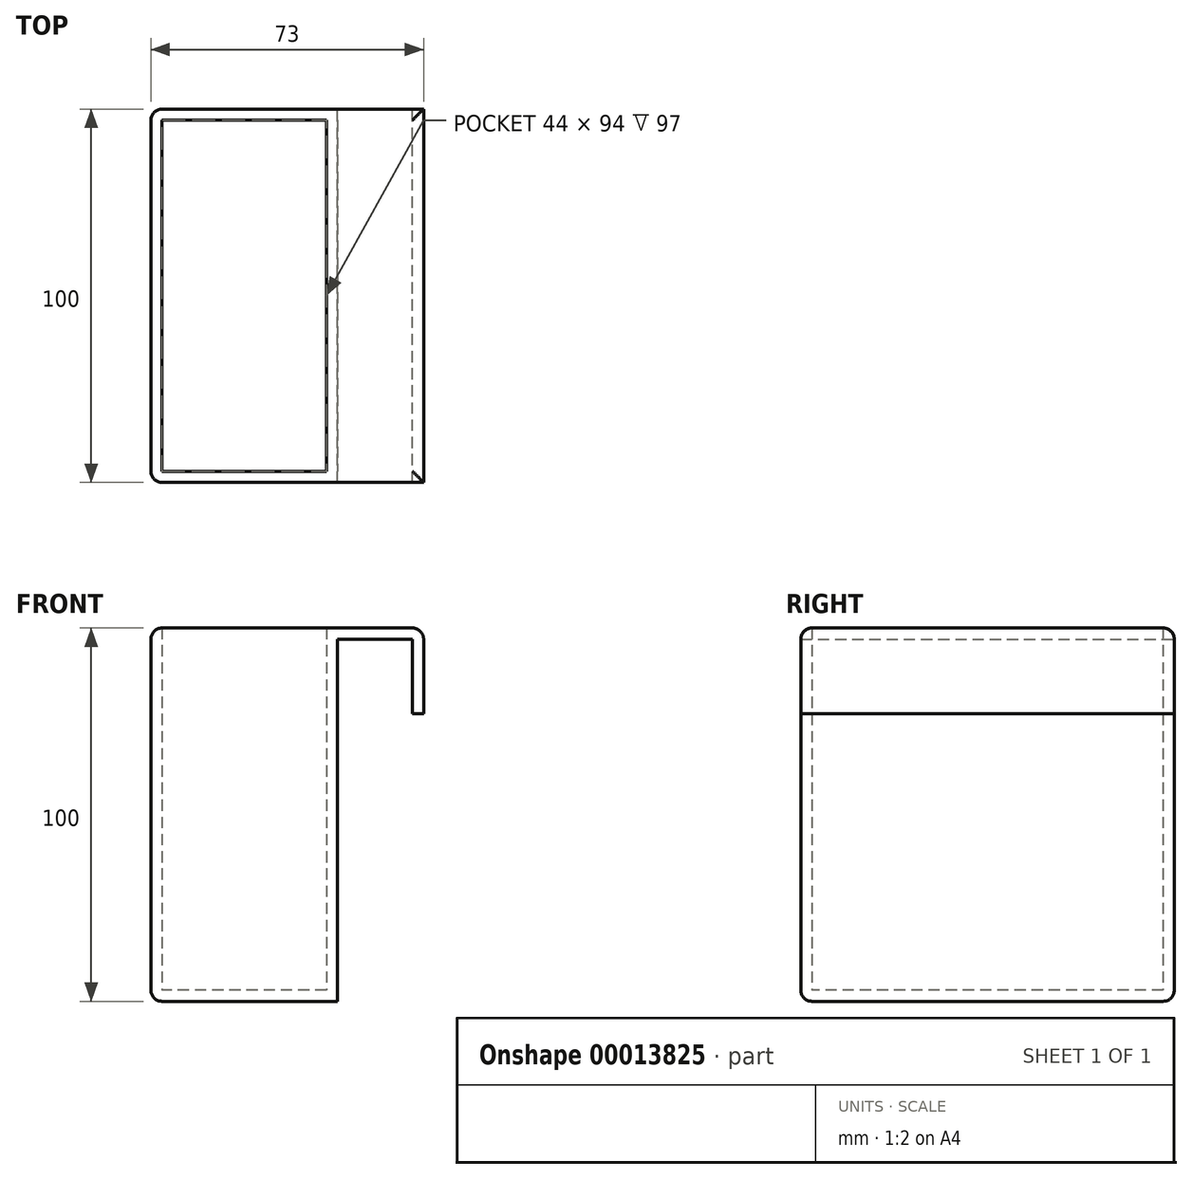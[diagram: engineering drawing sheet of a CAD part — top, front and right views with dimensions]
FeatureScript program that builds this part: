
annotation { "Feature Type Name" : "Feature", "Feature Type Description" : "" }
export const myFeature = defineFeature(function(context is Context, id is Id, definition is map)
    precondition{}
    {
        {
            var Q0;
            Q0=qCreatedBy(makeId("Top.planeOp"),FACE);
            var sketch = newSketch(context, id + "F0", { "sketchPlane" : qUnion([Q0])});
            skLineSegment(sketch, "E0.bottom", {"start": v(0, 0) * mm, "end": v(-50, 0) * mm});
            skLineSegment(sketch, "E0.top", {"start": v(0, -100) * mm, "end": v(-50, -100) * mm});
            skLineSegment(sketch, "E0.left", {"start": v(0, 0) * mm, "end": v(0, -100) * mm});
            skLineSegment(sketch, "E0.right", {"start": v(-50, 0) * mm, "end": v(-50, -100) * mm});
            skSolve(sketch);
        }
        {
            var Q0;
            Q0=makeQuery(id+"F0.imprint","IMPRINT",FACE,{"disambiguationData":[TD([[makeQuery(id+"F0.imprint","IMPRINT",EDGE,{"derivedFrom":sQuery(id+"F0.wireOp",EDGE,"E0.bottom")}),1.0]])]});
            extrude(context, id + "F1", {"entities" : qUnion([Q0]), "depth" : 100 * mm});
        }
        {
            var Q0;
            Q0=makeQuery(id+"F1.opExtrude","CAP_FACE",FACE,{"disambiguationData":[OSD([sQuery(id+"F0.wireOp",EDGE,"E0.bottom"),sQuery(id+"F0.wireOp",EDGE,"E0.top"),sQuery(id+"F0.wireOp",EDGE,"E0.left"),sQuery(id+"F0.wireOp",EDGE,"E0.right")])],"isStart":false});
            shell(context, id + "F2", {"entities" : qUnion([Q0]), "thickness" : 3 * mm});
        }
        {
            var Q0;
            Q0=makeQuery(id+"F1.opExtrude","SWEPT_FACE",FACE,{"disambiguationData":[OSD([sQuery(id+"F0.wireOp",EDGE,"E0.left")])]});
            var sketch = newSketch(context, id + "F3", { "sketchPlane" : qUnion([Q0])});
            skLineSegment(sketch, "E1.bottom", {"start": v(-100, 100) * mm, "end": v(0, 100) * mm});
            skLineSegment(sketch, "E1.top", {"start": v(-100, 97) * mm, "end": v(0, 97) * mm});
            skLineSegment(sketch, "E1.left", {"start": v(-100, 100) * mm, "end": v(-100, 97) * mm});
            skLineSegment(sketch, "E1.right", {"start": v(0, 100) * mm, "end": v(0, 97) * mm});
            skSolve(sketch);
        }
        {
            var Q0;
            Q0 = qSketchRegion(id + "F3", true);
            extrude(context, id + "F4", {"entities" : qUnion([Q0]), "operationType" : NewBodyOperationType.ADD, "depth" : 23 * mm});
        }
        {
            var Q0;
            Q0=makeQuery(id+"F4.opExtrude","SWEPT_FACE",FACE,{"disambiguationData":[OSD([sQuery(id+"F3.wireOp",EDGE,"E1.top")])]});
            var sketch = newSketch(context, id + "F5", { "sketchPlane" : qUnion([Q0])});
            skLineSegment(sketch, "E2.bottom", {"start": v(23, 100) * mm, "end": v(20, 100) * mm});
            skLineSegment(sketch, "E2.top", {"start": v(23, 0) * mm, "end": v(20, 0) * mm});
            skLineSegment(sketch, "E2.left", {"start": v(23, 100) * mm, "end": v(23, 0) * mm});
            skLineSegment(sketch, "E2.right", {"start": v(20, 100) * mm, "end": v(20, 0) * mm});
            skSolve(sketch);
        }
        {
            var Q0;
            Q0=makeQuery(id+"F5.imprint","IMPRINT",FACE,{"disambiguationData":[TD([[makeQuery(id+"F5.imprint","IMPRINT",EDGE,{"derivedFrom":sQuery(id+"F5.wireOp",EDGE,"E2.bottom")}),1.0]])]});
            extrude(context, id + "F6", {"entities" : qUnion([Q0]), "operationType" : NewBodyOperationType.ADD, "depth" : 20 * mm});
        }
        {
            var Q0;
            Q0=makeQuery(id+"F1.opExtrude","SWEPT_EDGE",EDGE,{"disambiguationData":[OSD([sQuery(id+"F0.wireOp",EDGE,"E0.top"),sQuery(id+"F0.wireOp",EDGE,"E0.right")])]});
            var Q1;
            Q1=makeQuery(id+"F1.opExtrude","SWEPT_EDGE",EDGE,{"disambiguationData":[OSD([sQuery(id+"F0.wireOp",EDGE,"E0.bottom"),sQuery(id+"F0.wireOp",EDGE,"E0.right")])]});
            var Q2;
            Q2=makeQuery(id+"F1.opExtrude","CAP_EDGE",EDGE,{"disambiguationData":[OSD([sQuery(id+"F0.wireOp",EDGE,"E0.right")])],"isStart":true});
            var Q3;
            Q3=makeQuery(id+"F1.opExtrude","CAP_EDGE",EDGE,{"disambiguationData":[OSD([sQuery(id+"F0.wireOp",EDGE,"E0.top")])],"isStart":true});
            var Q4;
            Q4=makeQuery(id+"F1.opExtrude","CAP_EDGE",EDGE,{"disambiguationData":[OSD([sQuery(id+"F0.wireOp",EDGE,"E0.bottom")])],"isStart":true});
            var Q5;
            Q5=makeQuery(id+"F1.opExtrude","CAP_EDGE",EDGE,{"disambiguationData":[OSD([sQuery(id+"F0.wireOp",EDGE,"E0.right")])],"isStart":false});
            var Q6;
            Q6=makeQuery(id+"F4.boolean.opBoolean","MERGE",EDGE,{"derivedFrom":[makeQuery(id+"F1.opExtrude","CAP_EDGE",EDGE,{"disambiguationData":[OSD([sQuery(id+"F0.wireOp",EDGE,"E0.bottom")])],"isStart":false}),makeQuery(id+"F4.opExtrude","SWEPT_EDGE",EDGE,{"disambiguationData":[OSD([sQuery(id+"F3.wireOp",EDGE,"E1.bottom"),sQuery(id+"F3.wireOp",EDGE,"E1.right")])]})]});
            var Q7;
            Q7=makeQuery(id+"F4.opExtrude","CAP_EDGE",EDGE,{"disambiguationData":[OSD([sQuery(id+"F3.wireOp",EDGE,"E1.bottom")])],"isStart":false});
            var Q8;
            Q8=makeQuery(id+"F4.boolean.opBoolean","MERGE",EDGE,{"derivedFrom":[makeQuery(id+"F1.opExtrude","CAP_EDGE",EDGE,{"disambiguationData":[OSD([sQuery(id+"F0.wireOp",EDGE,"E0.top")])],"isStart":false}),makeQuery(id+"F4.opExtrude","SWEPT_EDGE",EDGE,{"disambiguationData":[OSD([sQuery(id+"F3.wireOp",EDGE,"E1.bottom"),sQuery(id+"F3.wireOp",EDGE,"E1.left")])]})]});
            fillet(context, id + "F7", {"entities" : qUnion([Q0, Q1, Q2, Q3, Q4, Q5, Q6, Q7, Q8]), "radius" : 3 * mm, "tangentPropagation" : true, "allowEdgeOverflow" : false});
        }
    });
